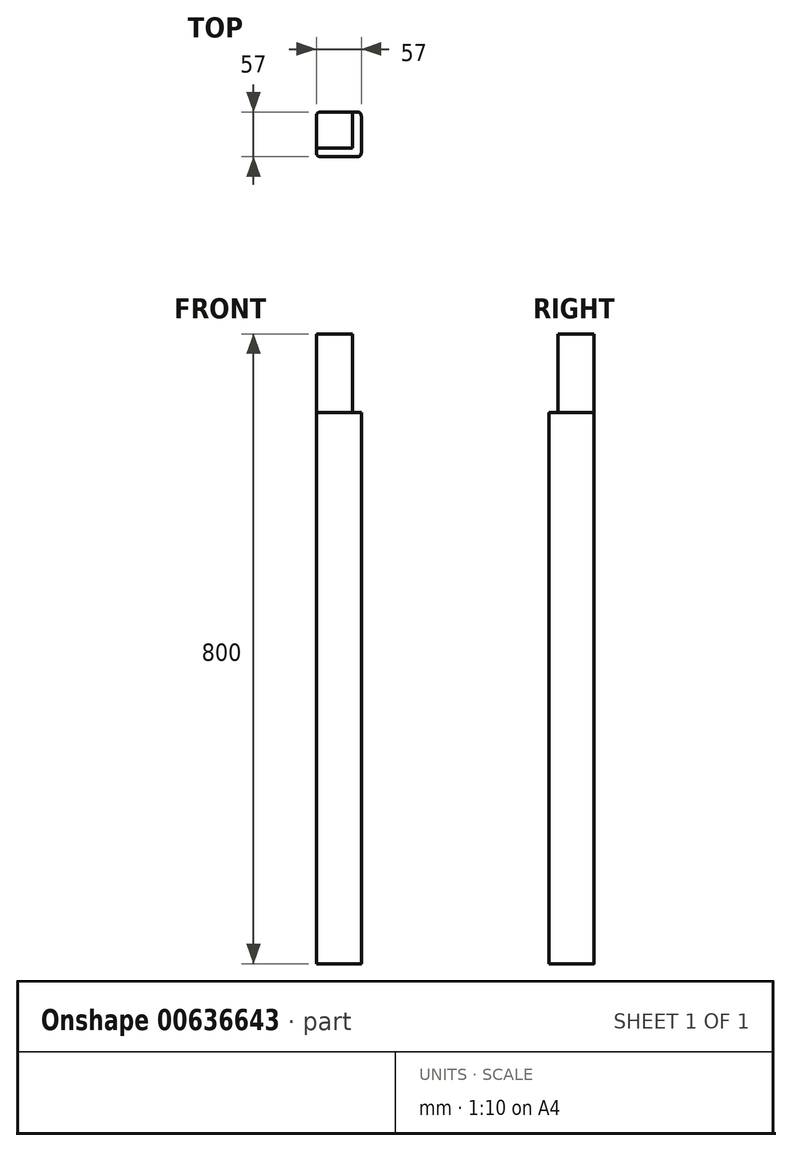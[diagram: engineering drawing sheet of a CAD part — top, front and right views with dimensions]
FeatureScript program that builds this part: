
annotation { "Feature Type Name" : "Feature", "Feature Type Description" : "" }
export const myFeature = defineFeature(function(context is Context, id is Id, definition is map)
    precondition{}
    {
        {
            var Q0;
            Q0=qCreatedBy(makeId("Top.planeOp"),FACE);
            var sketch = newSketch(context, id + "F0", { "sketchPlane" : qUnion([Q0])});
            skLineSegment(sketch, "E0.bottom", {"start": v(-23.5, 28.5) * mm, "end": v(23.5, 28.5) * mm});
            skLineSegment(sketch, "E0.top", {"start": v(-23.5, -28.5) * mm, "end": v(23.5, -28.5) * mm});
            skLineSegment(sketch, "E0.left", {"start": v(-28.5, 23.5) * mm, "end": v(-28.5, -23.5) * mm});
            skLineSegment(sketch, "E0.right", {"start": v(28.5, 23.5) * mm, "end": v(28.5, -23.5) * mm});
            skPoint(sketch, "E1.visualSharp", {"position": v(-28.5, 28.5) * mm});
            skArc(sketch, "E1.filletArc", {"start": v(-23.5, 28.5) * mm, "mid": v(-27.04, 27.04) * mm, "end": v(-28.5, 23.5) * mm});
            skPoint(sketch, "E2.visualSharp", {"position": v(28.5, 28.5) * mm});
            skArc(sketch, "E2.filletArc", {"start": v(28.5, 23.5) * mm, "mid": v(27.04, 27.04) * mm, "end": v(23.5, 28.5) * mm});
            skPoint(sketch, "E3.visualSharp", {"position": v(28.5, -28.5) * mm});
            skArc(sketch, "E3.filletArc", {"start": v(23.5, -28.5) * mm, "mid": v(27.04, -27.04) * mm, "end": v(28.5, -23.5) * mm});
            skPoint(sketch, "E4.visualSharp", {"position": v(-28.5, -28.5) * mm});
            skArc(sketch, "E4.filletArc", {"start": v(-28.5, -23.5) * mm, "mid": v(-27.04, -27.04) * mm, "end": v(-23.5, -28.5) * mm});
            skSolve(sketch);
        }
        {
            var Q0;
            Q0=qSketchRegion(id+"F0",true);
            extrude(context, id + "F1", {"entities" : qUnion([Q0]), "depth" : 800 * mm, "offsetDistance" : 25 * mm});
        }
        {
            var Q0;
            Q0=makeQuery(id+"F1.opExtrude","CAP_FACE",FACE,{"disambiguationData":[OSD([sQuery(id+"F0.wireOp",EDGE,"E0.bottom"),sQuery(id+"F0.wireOp",EDGE,"E0.top"),sQuery(id+"F0.wireOp",EDGE,"E0.left"),sQuery(id+"F0.wireOp",EDGE,"E0.right"),sQuery(id+"F0.wireOp",EDGE,"E1.filletArc"),sQuery(id+"F0.wireOp",EDGE,"E2.filletArc"),sQuery(id+"F0.wireOp",EDGE,"E3.filletArc"),sQuery(id+"F0.wireOp",EDGE,"E4.filletArc")])],"isStart":false});
            var sketch = newSketch(context, id + "F2", { "sketchPlane" : qUnion([Q0])});
            skLineSegment(sketch, "E5.bottom", {"start": v(-35.62, -32.5) * mm, "end": v(32.5, -32.5) * mm});
            skLineSegment(sketch, "E5.top", {"start": v(-35.62, -17.5) * mm, "end": v(17.5, -17.5) * mm});
            skLineSegment(sketch, "E5.left", {"start": v(-35.62, -32.5) * mm, "end": v(-35.62, -17.5) * mm});
            skLineSegment(sketch, "E6", {"start": v(17.5, -17.5) * mm, "end": v(17.5, 34.95) * mm});
            skLineSegment(sketch, "E7", {"start": v(17.5, 34.95) * mm, "end": v(32.5, 34.95) * mm});
            skLineSegment(sketch, "E8", {"start": v(32.5, 34.95) * mm, "end": v(32.5, -32.5) * mm});
            skSolve(sketch);
        }
        {
            var Q0;
            Q0=qSketchRegion(id+"F2",true);
            extrude(context, id + "F3", {"entities" : qUnion([Q0]), "operationType" : NewBodyOperationType.REMOVE, "oppositeDirection" : true, "depth" : 100 * mm, "offsetDistance" : 25 * mm});
        }
    });
